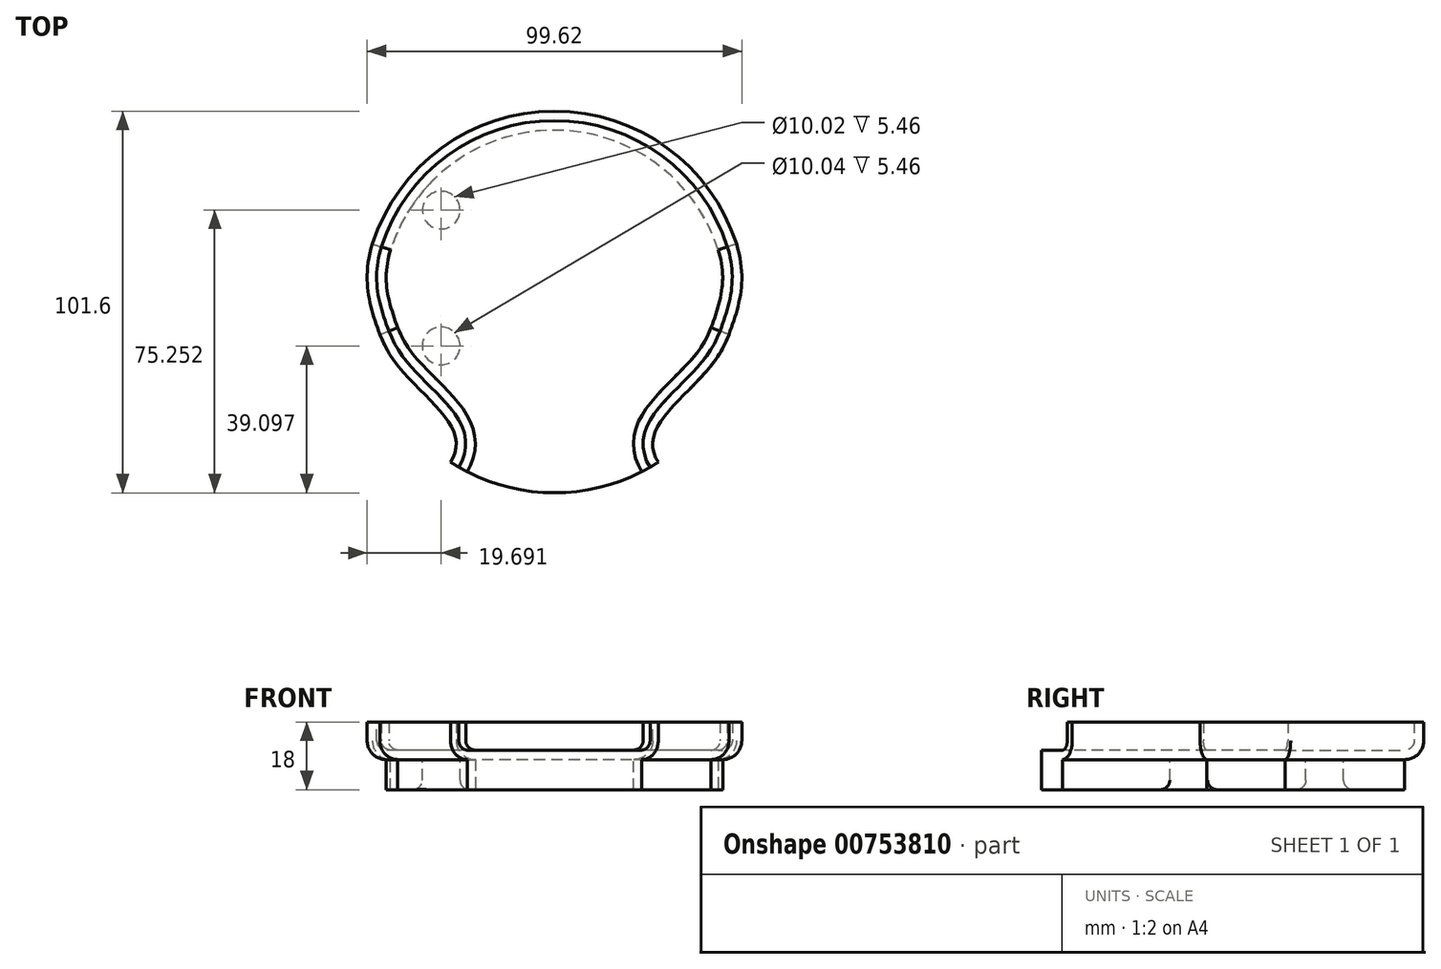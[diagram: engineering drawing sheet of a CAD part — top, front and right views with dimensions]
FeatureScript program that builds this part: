
annotation { "Feature Type Name" : "Feature", "Feature Type Description" : "" }
export const myFeature = defineFeature(function(context is Context, id is Id, definition is map)
    precondition{}
    {
        {
            var Q0;
            Q0=qCreatedBy(makeId("Top.planeOp"),FACE);
            var sketch = newSketch(context, id + "F0", { "sketchPlane" : qUnion([Q0])});
            skCircle(sketch, "E0", {"center": v(0, 0) * mm, "radius": 50.8 * mm});
            skLineSegment(sketch, "E1", {"start": v(0, 0) * mm, "end": v(0, -37.48) * mm});
            skFitSpline(sketch, "E2", {"points": [v(50.8, 0) * mm, v(43.94, -13.7) * mm, v(26.27, -36.2) * mm, v(33.75, -46.44) * mm, v(56.35, -23.6) * mm, v(50.8, 0) * mm]});
            skFitSpline(sketch, "E3", {"points": [v(46.4, -8.66) * mm, v(48.4, 15.4) * mm, v(40.4, 36.22) * mm, v(66.98, 9.9) * mm, v(55.4, 15.34) * mm, v(54.19, -4.27) * mm], "startDerivative": vector(36.46, 102.33) * mm, "endDerivative": vector(27.24, -157.84) * mm});
            skFitSpline(sketch, "E4.MirrorC", {"points": [v(-50.8, 0) * mm, v(-43.94, -13.7) * mm, v(-26.27, -36.2) * mm, v(-33.75, -46.44) * mm, v(-56.35, -23.6) * mm, v(-50.8, 0) * mm]});
            skFitSpline(sketch, "E5.MirrorCS", {"points": [v(-46.4, -8.66) * mm, v(-48.4, 15.4) * mm, v(-40.4, 36.22) * mm, v(-66.98, 9.9) * mm, v(-55.4, 15.34) * mm, v(-54.19, -4.27) * mm], "startDerivative": vector(-36.46, 102.33) * mm, "endDerivative": vector(-27.24, -157.84) * mm});
            skSolve(sketch);
        }
        {
            var Q0;
            {var subQ0=sQuery(id+"F0.wireOp",EDGE,"E3");var subQ3=sQuery(id+"F0.wireOp",EDGE,"E0");var subQ4=makeQuery(id+"F0.imprint","INTERSECT",VERTEX,{"derivedFrom":[subQ3,subQ0]});Q0=makeQuery(id+"F0.imprint","IMPRINT",FACE,{"disambiguationData":[TD([[makeQuery(id+"F0.imprint","IMPRINT",EDGE,{"disambiguationData":[TD([[subQ4,-1.0]])],"derivedFrom":subQ3}),1.0]])]});}
            extrude(context, id + "F1", {"entities" : qUnion([Q0]), "depth" : 10 * mm, "offsetDistance" : 25.4 * mm});
        }
        {
            var Q0;
            Q0=makeQuery(id+"F1.opExtrude","CAP_EDGE",EDGE,{"disambiguationData":[OSD([sQuery(id+"F0.wireOp",EDGE,"E2")])],"isStart":true});
            var Q1;
            Q1=makeQuery(id+"F1.opExtrude","CAP_EDGE",EDGE,{"disambiguationData":[OSD([sQuery(id+"F0.wireOp",EDGE,"E3")])],"isStart":true});
            var Q2;
            {var subQ0=sQuery(id+"F0.wireOp",EDGE,"E0");Q2=makeQuery(id+"F1.opExtrude","CAP_EDGE",EDGE,{"disambiguationData":[OSD([subQ0]),TDD([makeQuery(id+"F0.imprint","IMPRINT",EDGE,{"disambiguationData":[TD([[makeQuery(id+"F0.imprint","INTERSECT",VERTEX,{"derivedFrom":[subQ0,sQuery(id+"F0.wireOp",EDGE,"E3")]}),-1.0]])],"derivedFrom":subQ0})])],"isStart":true});}
            var Q3;
            Q3=makeQuery(id+"F1.opExtrude","CAP_EDGE",EDGE,{"disambiguationData":[OSD([sQuery(id+"F0.wireOp",EDGE,"E5.MirrorCS")])],"isStart":true});
            var Q4;
            Q4=makeQuery(id+"F1.opExtrude","CAP_EDGE",EDGE,{"disambiguationData":[OSD([sQuery(id+"F0.wireOp",EDGE,"E4.MirrorC")])],"isStart":true});
            fillet(context, id + "F2", {"entities" : qUnion([Q0, Q1, Q2, Q3, Q4]), "radius" : 5.08 * mm, "tangentPropagation" : true, "allowEdgeOverflow" : false});
        }
        {
            var Q0;
            {var subQ0=sQuery(id+"F0.wireOp",EDGE,"E0");Q0=makeQuery(id+"F1.opExtrude","SWEPT_FACE",FACE,{"disambiguationData":[OSD([subQ0]),TDD([makeQuery(id+"F0.imprint","IMPRINT",EDGE,{"disambiguationData":[TD([[makeQuery(id+"F0.imprint","INTERSECT",VERTEX,{"disambiguationData":[OD(0.0)],"derivedFrom":[subQ0,sQuery(id+"F0.wireOp",EDGE,"E4.MirrorC")]}),-1.0]])],"derivedFrom":subQ0})])]});}
            var Q1;
            Q1=makeQuery(id+"F1.opExtrude","CAP_FACE",FACE,{"disambiguationData":[OSD([sQuery(id+"F0.wireOp",EDGE,"E0"),sQuery(id+"F0.wireOp",EDGE,"E2"),sQuery(id+"F0.wireOp",EDGE,"E3"),sQuery(id+"F0.wireOp",EDGE,"E4.MirrorC"),sQuery(id+"F0.wireOp",EDGE,"E5.MirrorCS")])],"isStart":false});
            shell(context, id + "F3", {"entities" : qUnion([Q0, Q1]), "thickness" : 2.54 * mm});
        }
        {
            var Q0;
            Q0=makeQuery(id+"F1.opExtrude","CAP_FACE",FACE,{"disambiguationData":[OSD([sQuery(id+"F0.wireOp",EDGE,"E0"),sQuery(id+"F0.wireOp",EDGE,"E2"),sQuery(id+"F0.wireOp",EDGE,"E3"),sQuery(id+"F0.wireOp",EDGE,"E4.MirrorC"),sQuery(id+"F0.wireOp",EDGE,"E5.MirrorCS")])],"isStart":true});
            var sketch = newSketch(context, id + "F4", { "sketchPlane" : qUnion([Q0])});
            skCircle(sketch, "E6", {"center": v(30.12, -24.45) * mm, "radius": 5 * mm});
            skCircle(sketch, "E7", {"center": v(30.12, 11.7) * mm, "radius": 5.02 * mm});
            skLineSegment(sketch, "E8", {"start": v(0, 0) * mm, "end": v(0, 11.49) * mm});
            skCircle(sketch, "E9.MirrorC", {"center": v(-30.12, 11.7) * mm, "radius": 5.02 * mm});
            skCircle(sketch, "E10.MirrorC", {"center": v(-30.12, -24.45) * mm, "radius": 5 * mm});
            skSolve(sketch);
        }
        {
            var Q0;
            Q0=makeQuery(id+"F4.imprint","IMPRINT",FACE,{"disambiguationData":[TD([[makeQuery(id+"F4.imprint","IMPRINT",EDGE,{"derivedFrom":sQuery(id+"F4.wireOp",EDGE,"E7")}),1.0]])]});
            var Q1;
            Q1=makeQuery(id+"F4.imprint","IMPRINT",FACE,{"disambiguationData":[TD([[makeQuery(id+"F4.imprint","IMPRINT",EDGE,{"derivedFrom":sQuery(id+"F4.wireOp",EDGE,"E6")}),1.0]])]});
            var Q2;
            Q2=makeQuery(id+"F4.imprint","IMPRINT",FACE,{"disambiguationData":[TD([[makeQuery(id+"F4.imprint","IMPRINT",EDGE,{"derivedFrom":sQuery(id+"F4.wireOp",EDGE,"E9.MirrorC")}),-1.0]])]});
            var Q3;
            Q3=makeQuery(id+"F4.imprint","IMPRINT",FACE,{"disambiguationData":[TD([[makeQuery(id+"F4.imprint","IMPRINT",EDGE,{"derivedFrom":sQuery(id+"F4.wireOp",EDGE,"E10.MirrorC")}),-1.0]])]});
            extrude(context, id + "F5", {"entities" : qUnion([Q0, Q1, Q2, Q3]), "operationType" : NewBodyOperationType.ADD, "depth" : 8 * mm, "offsetDistance" : 25.4 * mm});
        }
        {
            var Q0;
            Q0=makeQuery(id+"F5.opExtrude","CAP_EDGE",EDGE,{"disambiguationData":[OSD([sQuery(id+"F4.wireOp",EDGE,"E7")])],"isStart":false});
            var Q1;
            Q1=makeQuery(id+"F5.opExtrude","CAP_EDGE",EDGE,{"disambiguationData":[OSD([sQuery(id+"F4.wireOp",EDGE,"E6")])],"isStart":false});
            var Q2;
            Q2=makeQuery(id+"F5.opExtrude","CAP_EDGE",EDGE,{"disambiguationData":[OSD([sQuery(id+"F4.wireOp",EDGE,"E10.MirrorC")])],"isStart":false});
            var Q3;
            Q3=makeQuery(id+"F5.opExtrude","CAP_EDGE",EDGE,{"disambiguationData":[OSD([sQuery(id+"F4.wireOp",EDGE,"E9.MirrorC")])],"isStart":false});
            fillet(context, id + "F6", {"entities" : qUnion([Q0, Q1, Q2, Q3]), "radius" : 2.54 * mm, "tangentPropagation" : true, "allowEdgeOverflow" : false});
        }
    });
